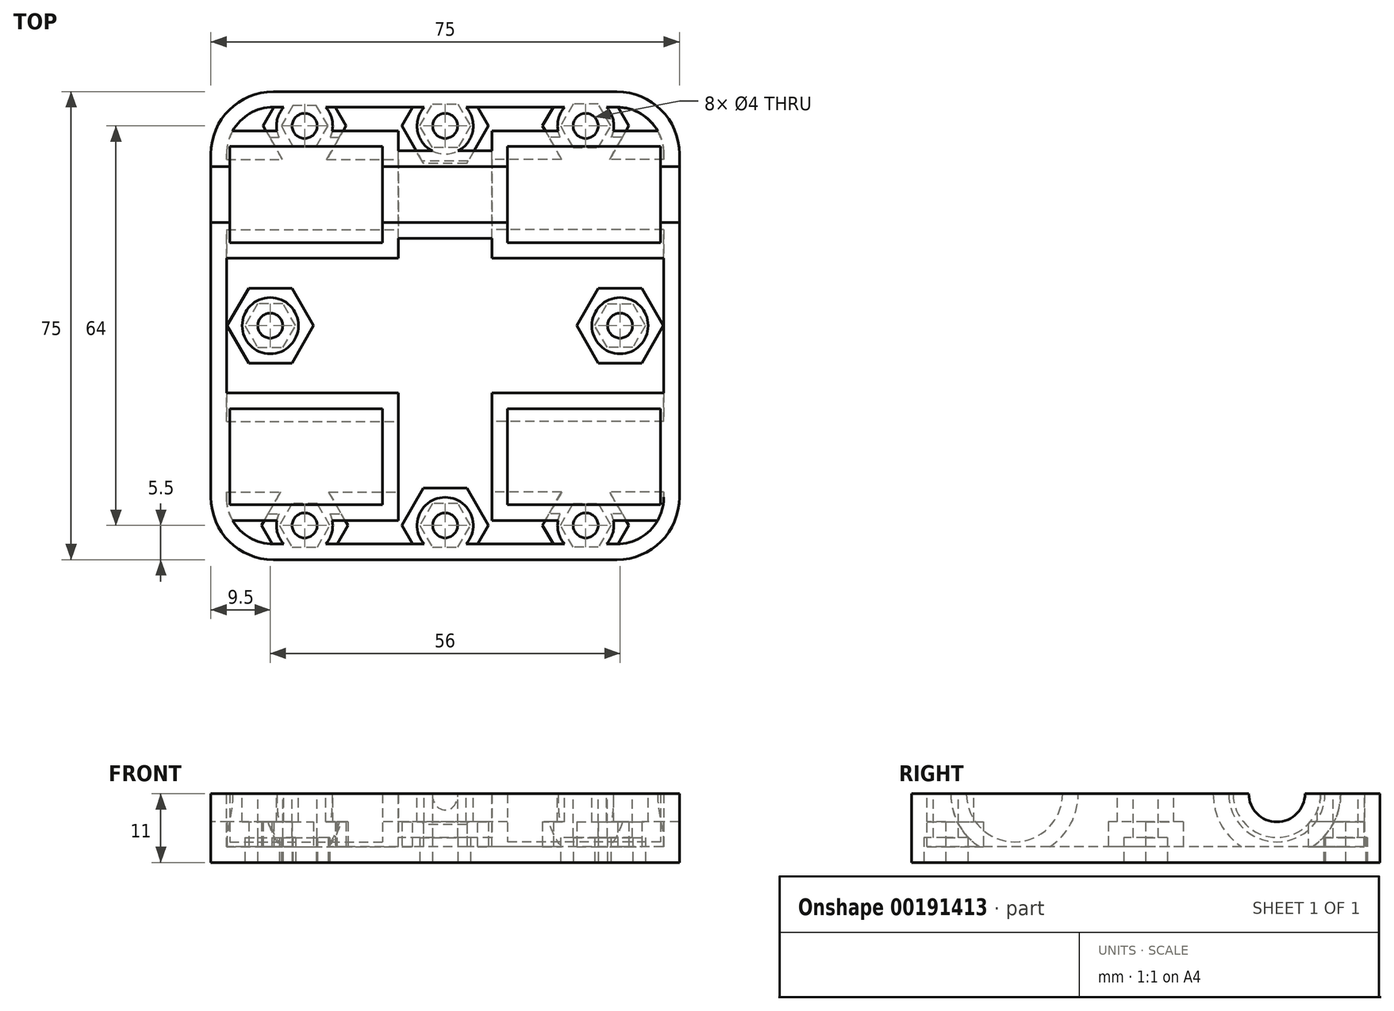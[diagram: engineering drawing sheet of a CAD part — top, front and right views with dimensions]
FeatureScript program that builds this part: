
annotation { "Feature Type Name" : "Feature", "Feature Type Description" : "" }
export const myFeature = defineFeature(function(context is Context, id is Id, definition is map)
    precondition{}
    {
        {
            var Q0;
            Q0=qCreatedBy(makeId("Top.planeOp"),FACE);
            var sketch = newSketch(context, id + "F0", { "sketchPlane" : qUnion([Q0])});
            skLineSegment(sketch, "E0.bottom", {"start": v(37.5, 37.5) * mm, "end": v(-37.5, 37.5) * mm});
            skLineSegment(sketch, "E0.top", {"start": v(37.5, -37.5) * mm, "end": v(-37.5, -37.5) * mm});
            skLineSegment(sketch, "E0.left", {"start": v(37.5, 37.5) * mm, "end": v(37.5, -37.5) * mm});
            skLineSegment(sketch, "E0.right", {"start": v(-37.5, 37.5) * mm, "end": v(-37.5, -37.5) * mm});
            skPoint(sketch, "E0.middle", {"position": v(0, 0) * mm});
            skSolve(sketch);
        }
        {
            var Q0;
            Q0 = qSketchRegion(id + "F0", true);
            extrude(context, id + "F1", {"entities" : qUnion([Q0]), "depth" : 11 * mm});
        }
        {
            var Q0;
            Q0=qCreatedBy(makeId("Right.planeOp"),FACE);
            cPlane(context, id + "F2", {"entities" : qUnion([Q0]), "cplaneType" : CPlaneType.OFFSET, "offset" : 10 * mm, "width" : 150 * mm, "height" : 150 * mm});
        }
        {
            var Q0;
            Q0=qCreatedBy(id+"F2.planeOp",FACE);
            var sketch = newSketch(context, id + "F3", { "sketchPlane" : qUnion([Q0])});
            skLineSegment(sketch, "E1", {"start": v(-21, 26.8) * mm, "end": v(-21, -8.17) * mm, "construction": true});
            skLineSegment(sketch, "E2.MirrorCS", {"start": v(21, 26.8) * mm, "end": v(21, -8.17) * mm, "construction": true});
            skCircle(sketch, "E3", {"center": v(-21, 11) * mm, "radius": 7.7 * mm});
            skCircle(sketch, "E4.MirrorC", {"center": v(21, 11) * mm, "radius": 7.7 * mm});
            skSolve(sketch);
        }
        {
            var Q0;
            Q0 = qSketchRegion(id + "F3", true);
            extrude(context, id + "F4", {"entities" : qUnion([Q0]), "operationType" : NewBodyOperationType.REMOVE, "depth" : 24.5 * mm});
        }
        {
            var Q0;
            Q0=qCreatedBy(makeId("Right.planeOp"),FACE);
            cPlane(context, id + "F5", {"entities" : qUnion([Q0]), "cplaneType" : CPlaneType.OFFSET, "offset" : 10 * mm, "oppositeDirection" : true, "width" : 150 * mm, "height" : 150 * mm});
        }
        {
            var Q0;
            Q0=qCreatedBy(id+"F5.planeOp",FACE);
            var sketch = newSketch(context, id + "F6", { "sketchPlane" : qUnion([Q0])});
            skLineSegment(sketch, "E5", {"start": v(21, 27.18) * mm, "end": v(21, -19.17) * mm, "construction": true});
            skCircle(sketch, "E6", {"center": v(21, 11) * mm, "radius": 7.7 * mm});
            skCircle(sketch, "E7.MirrorC", {"center": v(-21, 11) * mm, "radius": 7.7 * mm});
            skSolve(sketch);
        }
        {
            var Q0;
            Q0 = qSketchRegion(id + "F6", true);
            extrude(context, id + "F7", {"entities" : qUnion([Q0]), "operationType" : NewBodyOperationType.REMOVE, "oppositeDirection" : true, "depth" : 24.5 * mm});
        }
        {
            var Q0;
            Q0=makeQuery(id+"F1.opExtrude","SWEPT_FACE",FACE,{"disambiguationData":[OSD([sQuery(id+"F0.wireOp",EDGE,"E0.right")])]});
            var sketch = newSketch(context, id + "F8", { "sketchPlane" : qUnion([Q0])});
            skLineSegment(sketch, "E8", {"start": v(-21, 26.36) * mm, "end": v(-21, 10.36) * mm, "construction": true});
            skCircle(sketch, "E9", {"center": v(-21, 11) * mm, "radius": 4.5 * mm});
            skPoint(sketch, "E9.centerSnap0", {"position": v(-21, 18.36) * mm});
            skLineSegment(sketch, "E10.MirrorCS", {"start": v(21, 26.36) * mm, "end": v(21, 10.36) * mm, "construction": true});
            skCircle(sketch, "E11.MirrorC", {"center": v(21, 11) * mm, "radius": 4.5 * mm});
            skSolve(sketch);
        }
        {
            var Q0;
            {var subQ0=sQuery(id+"F8.wireOp",EDGE,"E9");var subQ1=makeQuery(id+"F1.opExtrude","CAP_EDGE",EDGE,{"disambiguationData":[OSD([sQuery(id+"F0.wireOp",EDGE,"E0.right")])],"isStart":false});var subQ2=makeQuery(id+"F8.imprint","INTERSECT",VERTEX,{"disambiguationData":[OD(0.0)],"derivedFrom":[subQ1,subQ0]});Q0=makeQuery(id+"F8.imprint","IMPRINT",FACE,{"disambiguationData":[TD([[makeQuery(id+"F8.imprint","IMPRINT",EDGE,{"disambiguationData":[TD([[subQ2,1.0]])],"derivedFrom":subQ0}),1.0]])]});}
            var Q1;
            {var subQ0=sQuery(id+"F8.wireOp",EDGE,"E9");var subQ1=makeQuery(id+"F1.opExtrude","CAP_EDGE",EDGE,{"disambiguationData":[OSD([sQuery(id+"F0.wireOp",EDGE,"E0.right")])],"isStart":false});var subQ2=makeQuery(id+"F8.imprint","INTERSECT",VERTEX,{"disambiguationData":[OD(0.0)],"derivedFrom":[subQ1,subQ0]});Q1=makeQuery(id+"F8.imprint","IMPRINT",FACE,{"disambiguationData":[TD([[makeQuery(id+"F8.imprint","IMPRINT",EDGE,{"disambiguationData":[TD([[subQ2,-1.0]])],"derivedFrom":subQ0}),1.0]])]});}
            var Q2;
            {var subQ0=sQuery(id+"F8.wireOp",EDGE,"E11.MirrorC");var subQ1=makeQuery(id+"F1.opExtrude","CAP_EDGE",EDGE,{"disambiguationData":[OSD([sQuery(id+"F0.wireOp",EDGE,"E0.right")])],"isStart":false});var subQ2=makeQuery(id+"F8.imprint","INTERSECT",VERTEX,{"disambiguationData":[OD(0.0)],"derivedFrom":[subQ1,subQ0]});Q2=makeQuery(id+"F8.imprint","IMPRINT",FACE,{"disambiguationData":[TD([[makeQuery(id+"F8.imprint","IMPRINT",EDGE,{"disambiguationData":[TD([[subQ2,-1.0]])],"derivedFrom":subQ0}),-1.0]])]});}
            extrude(context, id + "F9", {"entities" : qUnion([Q0, Q1, Q2]), "operationType" : NewBodyOperationType.REMOVE, "endBound" : BoundingType.THROUGH_ALL, "oppositeDirection" : true, "depth" : 25 * mm});
        }
        {
            var Q0;
            {var subQ0=sQuery(id+"F6.wireOp",EDGE,"E6");var subQ1=sQuery(id+"F3.wireOp",EDGE,"E4.MirrorC");var subQ2=sQuery(id+"F6.wireOp",EDGE,"E7.MirrorC");var subQ3=sQuery(id+"F3.wireOp",EDGE,"E3");var subQ4=sQuery(id+"F0.wireOp",EDGE,"E0.right");var subQ5=sQuery(id+"F0.wireOp",EDGE,"E0.left");Q0=makeQuery(id+"F9.boolean.opBoolean","SPLIT",FACE,{"disambiguationData":[TD([makeQuery(id+"F1.opExtrude","SWEPT_FACE",FACE,{"disambiguationData":[OSD([subQ5])]}),makeQuery(id+"F1.opExtrude","SWEPT_FACE",FACE,{"disambiguationData":[OSD([subQ4])]}),makeQuery(id+"F4.boolean.opBoolean","COPY",FACE,{"derivedFrom":makeQuery(id+"F4.opExtrude","SWEPT_FACE",FACE,{"disambiguationData":[OSD([subQ3])]})}),makeQuery(id+"F4.boolean.opBoolean","COPY",FACE,{"derivedFrom":makeQuery(id+"F4.opExtrude","CAP_FACE",FACE,{"disambiguationData":[OSD([subQ3])],"isStart":true})}),makeQuery(id+"F4.boolean.opBoolean","COPY",FACE,{"derivedFrom":makeQuery(id+"F4.opExtrude","CAP_FACE",FACE,{"disambiguationData":[OSD([subQ3])],"isStart":false})}),makeQuery(id+"F4.boolean.opBoolean","COPY",FACE,{"derivedFrom":makeQuery(id+"F4.opExtrude","SWEPT_FACE",FACE,{"disambiguationData":[OSD([subQ1])]})}),makeQuery(id+"F4.boolean.opBoolean","COPY",FACE,{"derivedFrom":makeQuery(id+"F4.opExtrude","CAP_FACE",FACE,{"disambiguationData":[OSD([subQ1])],"isStart":true})}),makeQuery(id+"F4.boolean.opBoolean","COPY",FACE,{"derivedFrom":makeQuery(id+"F4.opExtrude","CAP_FACE",FACE,{"disambiguationData":[OSD([subQ1])],"isStart":false})}),makeQuery(id+"F7.boolean.opBoolean","COPY",FACE,{"derivedFrom":makeQuery(id+"F7.opExtrude","SWEPT_FACE",FACE,{"disambiguationData":[OSD([subQ0])]})}),makeQuery(id+"F7.boolean.opBoolean","COPY",FACE,{"derivedFrom":makeQuery(id+"F7.opExtrude","CAP_FACE",FACE,{"disambiguationData":[OSD([subQ0])],"isStart":true})}),makeQuery(id+"F7.boolean.opBoolean","COPY",FACE,{"derivedFrom":makeQuery(id+"F7.opExtrude","CAP_FACE",FACE,{"disambiguationData":[OSD([subQ0])],"isStart":false})}),makeQuery(id+"F7.boolean.opBoolean","COPY",FACE,{"derivedFrom":makeQuery(id+"F7.opExtrude","SWEPT_FACE",FACE,{"disambiguationData":[OSD([subQ2])]})}),makeQuery(id+"F7.boolean.opBoolean","COPY",FACE,{"derivedFrom":makeQuery(id+"F7.opExtrude","CAP_FACE",FACE,{"disambiguationData":[OSD([subQ2])],"isStart":true})}),makeQuery(id+"F7.boolean.opBoolean","COPY",FACE,{"derivedFrom":makeQuery(id+"F7.opExtrude","CAP_FACE",FACE,{"disambiguationData":[OSD([subQ2])],"isStart":false})}),makeQuery(id+"F9.opExtrude","SWEPT_FACE",FACE,{"disambiguationData":[OSD([sQuery(id+"F8.wireOp",EDGE,"E9")])]}),makeQuery(id+"F9.opExtrude","SWEPT_FACE",FACE,{"disambiguationData":[OSD([sQuery(id+"F8.wireOp",EDGE,"E11.MirrorC")])]})])],"derivedFrom":makeQuery(id+"F1.opExtrude","CAP_FACE",FACE,{"disambiguationData":[OSD([sQuery(id+"F0.wireOp",EDGE,"E0.bottom"),sQuery(id+"F0.wireOp",EDGE,"E0.top"),subQ5,subQ4])],"isStart":false})});}
            var sketch = newSketch(context, id + "F10", { "sketchPlane" : qUnion([Q0])});
            skCircle(sketch, "E12", {"center": v(28, 0) * mm, "radius": 2 * mm});
            skCircle(sketch, "E13.MirrorC", {"center": v(-28, 0) * mm, "radius": 2 * mm});
            skCircle(sketch, "E14", {"center": v(0, -32) * mm, "radius": 2 * mm});
            skCircle(sketch, "E15.MirrorC", {"center": v(0, 32) * mm, "radius": 2 * mm});
            skCircle(sketch, "E16", {"center": v(-22.5, 32) * mm, "radius": 2 * mm});
            skCircle(sketch, "E17.MirrorC", {"center": v(22.5, 32) * mm, "radius": 2 * mm});
            skCircle(sketch, "E18.MirrorC", {"center": v(-22.5, -32) * mm, "radius": 2 * mm});
            skCircle(sketch, "E19.MirrorC", {"center": v(22.5, -32) * mm, "radius": 2 * mm});
            skSolve(sketch);
        }
        {
            var Q0;
            Q0 = qSketchRegion(id + "F10", true);
            extrude(context, id + "F11", {"entities" : qUnion([Q0]), "operationType" : NewBodyOperationType.REMOVE, "endBound" : BoundingType.THROUGH_ALL, "oppositeDirection" : true, "depth" : 25 * mm});
        }
        {
            var Q0;
            Q0=makeQuery(id+"F1.opExtrude","SWEPT_EDGE",EDGE,{"disambiguationData":[OSD([sQuery(id+"F0.wireOp",EDGE,"E0.bottom"),sQuery(id+"F0.wireOp",EDGE,"E0.left")])]});
            var Q1;
            Q1=makeQuery(id+"F1.opExtrude","SWEPT_EDGE",EDGE,{"disambiguationData":[OSD([sQuery(id+"F0.wireOp",EDGE,"E0.top"),sQuery(id+"F0.wireOp",EDGE,"E0.left")])]});
            var Q2;
            Q2=makeQuery(id+"F1.opExtrude","SWEPT_EDGE",EDGE,{"disambiguationData":[OSD([sQuery(id+"F0.wireOp",EDGE,"E0.top"),sQuery(id+"F0.wireOp",EDGE,"E0.right")])]});
            var Q3;
            Q3=makeQuery(id+"F1.opExtrude","SWEPT_EDGE",EDGE,{"disambiguationData":[OSD([sQuery(id+"F0.wireOp",EDGE,"E0.bottom"),sQuery(id+"F0.wireOp",EDGE,"E0.right")])]});
            fillet(context, id + "F12", {"entities" : qUnion([Q0, Q1, Q2, Q3]), "radius" : 10 * mm, "tangentPropagation" : true, "allowEdgeOverflow" : false});
        }
        {
            var Q0;
            Q0=makeQuery(id+"F1.opExtrude","CAP_FACE",FACE,{"disambiguationData":[OSD([sQuery(id+"F0.wireOp",EDGE,"E0.bottom"),sQuery(id+"F0.wireOp",EDGE,"E0.top"),sQuery(id+"F0.wireOp",EDGE,"E0.left"),sQuery(id+"F0.wireOp",EDGE,"E0.right")])],"isStart":true});
            var sketch = newSketch(context, id + "F13", { "sketchPlane" : qUnion([Q0])});
            skCircle(sketch, "E20.cCircle", {"center": v(-22.5, 32) * mm, "radius": 3.5 * mm, "construction": true});
            skLineSegment(sketch, "E20.0", {"start": v(-24.52, 35.5) * mm, "end": v(-20.48, 35.5) * mm});
            skLineSegment(sketch, "E20.1", {"start": v(-20.48, 35.5) * mm, "end": v(-18.46, 32) * mm});
            skLineSegment(sketch, "E20.2", {"start": v(-18.46, 32) * mm, "end": v(-20.48, 28.5) * mm});
            skLineSegment(sketch, "E20.3", {"start": v(-20.48, 28.5) * mm, "end": v(-24.52, 28.5) * mm});
            skLineSegment(sketch, "E20.4", {"start": v(-24.52, 28.5) * mm, "end": v(-26.54, 32) * mm});
            skLineSegment(sketch, "E20.5", {"start": v(-26.54, 32) * mm, "end": v(-24.52, 35.5) * mm});
            skPoint(sketch, "E20.0.midPoint", {"position": v(-22.5, 35.5) * mm});
            skLineSegment(sketch, "E21.MirrorCS", {"start": v(24.52, 35.5) * mm, "end": v(20.48, 35.5) * mm});
            skLineSegment(sketch, "E22.MirrorCS", {"start": v(26.54, 32) * mm, "end": v(24.52, 35.5) * mm});
            skLineSegment(sketch, "E23.MirrorCS", {"start": v(20.48, 28.5) * mm, "end": v(24.52, 28.5) * mm});
            skLineSegment(sketch, "E24.MirrorCS", {"start": v(18.46, 32) * mm, "end": v(20.48, 28.5) * mm});
            skCircle(sketch, "E25.MirrorC", {"center": v(22.5, 32) * mm, "radius": 3.5 * mm, "construction": true});
            skPoint(sketch, "E26.MirrorP", {"position": v(22.5, 35.5) * mm});
            skLineSegment(sketch, "E27.MirrorCS", {"start": v(24.52, 28.5) * mm, "end": v(26.54, 32) * mm});
            skLineSegment(sketch, "E28.MirrorCS", {"start": v(20.48, 35.5) * mm, "end": v(18.46, 32) * mm});
            skLineSegment(sketch, "E29.MirrorCS", {"start": v(24.52, -28.5) * mm, "end": v(26.54, -32) * mm});
            skLineSegment(sketch, "E30.MirrorCS", {"start": v(24.52, -35.5) * mm, "end": v(20.48, -35.5) * mm});
            skLineSegment(sketch, "E31.MirrorCS", {"start": v(18.46, -32) * mm, "end": v(20.48, -28.5) * mm});
            skLineSegment(sketch, "E32.MirrorCS", {"start": v(20.48, -28.5) * mm, "end": v(24.52, -28.5) * mm});
            skLineSegment(sketch, "E33.MirrorCS", {"start": v(26.54, -32) * mm, "end": v(24.52, -35.5) * mm});
            skLineSegment(sketch, "E34.MirrorCS", {"start": v(20.48, -35.5) * mm, "end": v(18.46, -32) * mm});
            skCircle(sketch, "E35.MirrorC", {"center": v(22.5, -32) * mm, "radius": 3.5 * mm, "construction": true});
            skPoint(sketch, "E36.MirrorP", {"position": v(22.5, -35.5) * mm});
            skCircle(sketch, "E37.cCircle", {"center": v(-22.5, -32) * mm, "radius": 3.25 * mm, "construction": true});
            skLineSegment(sketch, "E37.0", {"start": v(-24.38, -28.75) * mm, "end": v(-20.62, -28.75) * mm});
            skLineSegment(sketch, "E37.1", {"start": v(-20.62, -28.75) * mm, "end": v(-18.75, -32) * mm});
            skLineSegment(sketch, "E37.2", {"start": v(-18.75, -32) * mm, "end": v(-20.62, -35.25) * mm});
            skLineSegment(sketch, "E37.3", {"start": v(-20.62, -35.25) * mm, "end": v(-24.38, -35.25) * mm});
            skLineSegment(sketch, "E37.4", {"start": v(-24.38, -35.25) * mm, "end": v(-26.25, -32) * mm});
            skLineSegment(sketch, "E37.5", {"start": v(-26.25, -32) * mm, "end": v(-24.38, -28.75) * mm});
            skPoint(sketch, "E37.0.midPoint", {"position": v(-22.5, -28.75) * mm});
            skCircle(sketch, "E38.cCircle", {"center": v(0, 32) * mm, "radius": 3.5 * mm, "construction": true});
            skLineSegment(sketch, "E38.0", {"start": v(-2.02, 35.5) * mm, "end": v(2.02, 35.5) * mm});
            skLineSegment(sketch, "E38.1", {"start": v(2.02, 35.5) * mm, "end": v(4.04, 32) * mm});
            skLineSegment(sketch, "E38.2", {"start": v(4.04, 32) * mm, "end": v(2.02, 28.5) * mm});
            skLineSegment(sketch, "E38.3", {"start": v(2.02, 28.5) * mm, "end": v(-2.02, 28.5) * mm});
            skLineSegment(sketch, "E38.4", {"start": v(-2.02, 28.5) * mm, "end": v(-4.04, 32) * mm});
            skLineSegment(sketch, "E38.5", {"start": v(-4.04, 32) * mm, "end": v(-2.02, 35.5) * mm});
            skPoint(sketch, "E38.0.midPoint", {"position": v(0, 35.5) * mm});
            skCircle(sketch, "E39.cCircle", {"center": v(-28, 0) * mm, "radius": 3.5 * mm, "construction": true});
            skLineSegment(sketch, "E39.0", {"start": v(-30.02, 3.5) * mm, "end": v(-25.98, 3.5) * mm});
            skLineSegment(sketch, "E39.1", {"start": v(-25.98, 3.5) * mm, "end": v(-23.96, 0) * mm});
            skLineSegment(sketch, "E39.2", {"start": v(-23.96, 0) * mm, "end": v(-25.98, -3.5) * mm});
            skLineSegment(sketch, "E39.3", {"start": v(-25.98, -3.5) * mm, "end": v(-30.02, -3.5) * mm});
            skLineSegment(sketch, "E39.4", {"start": v(-30.02, -3.5) * mm, "end": v(-32.04, 0) * mm});
            skLineSegment(sketch, "E39.5", {"start": v(-32.04, 0) * mm, "end": v(-30.02, 3.5) * mm});
            skPoint(sketch, "E39.0.midPoint", {"position": v(-28, 3.5) * mm});
            skLineSegment(sketch, "E40.MirrorCS", {"start": v(30.02, 3.5) * mm, "end": v(25.98, 3.5) * mm});
            skLineSegment(sketch, "E41.MirrorCS", {"start": v(25.98, -3.5) * mm, "end": v(30.02, -3.5) * mm});
            skLineSegment(sketch, "E42.MirrorCS", {"start": v(30.02, -3.5) * mm, "end": v(32.04, 0) * mm});
            skLineSegment(sketch, "E43.MirrorCS", {"start": v(25.98, 3.5) * mm, "end": v(23.96, 0) * mm});
            skLineSegment(sketch, "E44.MirrorCS", {"start": v(23.96, 0) * mm, "end": v(25.98, -3.5) * mm});
            skLineSegment(sketch, "E45.MirrorCS", {"start": v(32.04, 0) * mm, "end": v(30.02, 3.5) * mm});
            skCircle(sketch, "E46.MirrorC", {"center": v(28, 0) * mm, "radius": 3.5 * mm, "construction": true});
            skPoint(sketch, "E47.MirrorP", {"position": v(28, 3.5) * mm});
            skLineSegment(sketch, "E48.MirrorCS", {"start": v(2.02, -35.5) * mm, "end": v(4.04, -32) * mm});
            skLineSegment(sketch, "E49.MirrorCS", {"start": v(2.02, -28.5) * mm, "end": v(-2.02, -28.5) * mm});
            skPoint(sketch, "E50.MirrorP", {"position": v(0, -35.5) * mm});
            skLineSegment(sketch, "E51.MirrorCS", {"start": v(-2.02, -28.5) * mm, "end": v(-4.04, -32) * mm});
            skCircle(sketch, "E52.MirrorC", {"center": v(0, -32) * mm, "radius": 3.5 * mm, "construction": true});
            skLineSegment(sketch, "E53.MirrorCS", {"start": v(-2.02, -35.5) * mm, "end": v(2.02, -35.5) * mm});
            skLineSegment(sketch, "E54.MirrorCS", {"start": v(-4.04, -32) * mm, "end": v(-2.02, -35.5) * mm});
            skLineSegment(sketch, "E55.MirrorCS", {"start": v(4.04, -32) * mm, "end": v(2.02, -28.5) * mm});
            skSolve(sketch);
        }
        {
            var Q0;
            Q0 = qSketchRegion(id + "F13", true);
            extrude(context, id + "F14", {"entities" : qUnion([Q0]), "operationType" : NewBodyOperationType.REMOVE, "oppositeDirection" : true, "depth" : 4 * mm});
        }
        {
            var Q0;
            {var subQ0=sQuery(id+"F3.wireOp",EDGE,"E4.MirrorC");var subQ1=sQuery(id+"F0.wireOp",EDGE,"E0.right");var subQ2=sQuery(id+"F0.wireOp",EDGE,"E0.left");var subQ3=sQuery(id+"F0.wireOp",EDGE,"E0.bottom");var subQ4=sQuery(id+"F6.wireOp",EDGE,"E6");Q0=makeQuery(id+"F9.boolean.opBoolean","SPLIT",FACE,{"disambiguationData":[TD([makeQuery(id+"F1.opExtrude","SWEPT_FACE",FACE,{"disambiguationData":[OSD([subQ3])]}),makeQuery(id+"F1.opExtrude","SWEPT_FACE",FACE,{"disambiguationData":[OSD([subQ2])]}),makeQuery(id+"F1.opExtrude","SWEPT_FACE",FACE,{"disambiguationData":[OSD([subQ1])]}),makeQuery(id+"F4.boolean.opBoolean","COPY",FACE,{"derivedFrom":makeQuery(id+"F4.opExtrude","SWEPT_FACE",FACE,{"disambiguationData":[OSD([subQ0])]})}),makeQuery(id+"F4.boolean.opBoolean","COPY",FACE,{"derivedFrom":makeQuery(id+"F4.opExtrude","CAP_FACE",FACE,{"disambiguationData":[OSD([subQ0])],"isStart":true})}),makeQuery(id+"F4.boolean.opBoolean","COPY",FACE,{"derivedFrom":makeQuery(id+"F4.opExtrude","CAP_FACE",FACE,{"disambiguationData":[OSD([subQ0])],"isStart":false})}),makeQuery(id+"F7.boolean.opBoolean","COPY",FACE,{"derivedFrom":makeQuery(id+"F7.opExtrude","SWEPT_FACE",FACE,{"disambiguationData":[OSD([subQ4])]})}),makeQuery(id+"F7.boolean.opBoolean","COPY",FACE,{"derivedFrom":makeQuery(id+"F7.opExtrude","CAP_FACE",FACE,{"disambiguationData":[OSD([subQ4])],"isStart":true})}),makeQuery(id+"F7.boolean.opBoolean","COPY",FACE,{"derivedFrom":makeQuery(id+"F7.opExtrude","CAP_FACE",FACE,{"disambiguationData":[OSD([subQ4])],"isStart":false})}),makeQuery(id+"F9.opExtrude","SWEPT_FACE",FACE,{"disambiguationData":[OSD([sQuery(id+"F8.wireOp",EDGE,"E9")])]})])],"derivedFrom":makeQuery(id+"F1.opExtrude","CAP_FACE",FACE,{"disambiguationData":[OSD([subQ3,sQuery(id+"F0.wireOp",EDGE,"E0.top"),subQ2,subQ1])],"isStart":false})});}
            var Q1;
            {var subQ0=sQuery(id+"F6.wireOp",EDGE,"E6");var subQ1=sQuery(id+"F3.wireOp",EDGE,"E4.MirrorC");var subQ2=sQuery(id+"F6.wireOp",EDGE,"E7.MirrorC");var subQ3=sQuery(id+"F3.wireOp",EDGE,"E3");var subQ4=sQuery(id+"F0.wireOp",EDGE,"E0.right");var subQ5=sQuery(id+"F0.wireOp",EDGE,"E0.left");Q1=makeQuery(id+"F9.boolean.opBoolean","SPLIT",FACE,{"disambiguationData":[TD([makeQuery(id+"F1.opExtrude","SWEPT_FACE",FACE,{"disambiguationData":[OSD([subQ5])]}),makeQuery(id+"F1.opExtrude","SWEPT_FACE",FACE,{"disambiguationData":[OSD([subQ4])]}),makeQuery(id+"F4.boolean.opBoolean","COPY",FACE,{"derivedFrom":makeQuery(id+"F4.opExtrude","SWEPT_FACE",FACE,{"disambiguationData":[OSD([subQ3])]})}),makeQuery(id+"F4.boolean.opBoolean","COPY",FACE,{"derivedFrom":makeQuery(id+"F4.opExtrude","CAP_FACE",FACE,{"disambiguationData":[OSD([subQ3])],"isStart":true})}),makeQuery(id+"F4.boolean.opBoolean","COPY",FACE,{"derivedFrom":makeQuery(id+"F4.opExtrude","CAP_FACE",FACE,{"disambiguationData":[OSD([subQ3])],"isStart":false})}),makeQuery(id+"F4.boolean.opBoolean","COPY",FACE,{"derivedFrom":makeQuery(id+"F4.opExtrude","SWEPT_FACE",FACE,{"disambiguationData":[OSD([subQ1])]})}),makeQuery(id+"F4.boolean.opBoolean","COPY",FACE,{"derivedFrom":makeQuery(id+"F4.opExtrude","CAP_FACE",FACE,{"disambiguationData":[OSD([subQ1])],"isStart":true})}),makeQuery(id+"F4.boolean.opBoolean","COPY",FACE,{"derivedFrom":makeQuery(id+"F4.opExtrude","CAP_FACE",FACE,{"disambiguationData":[OSD([subQ1])],"isStart":false})}),makeQuery(id+"F7.boolean.opBoolean","COPY",FACE,{"derivedFrom":makeQuery(id+"F7.opExtrude","SWEPT_FACE",FACE,{"disambiguationData":[OSD([subQ0])]})}),makeQuery(id+"F7.boolean.opBoolean","COPY",FACE,{"derivedFrom":makeQuery(id+"F7.opExtrude","CAP_FACE",FACE,{"disambiguationData":[OSD([subQ0])],"isStart":true})}),makeQuery(id+"F7.boolean.opBoolean","COPY",FACE,{"derivedFrom":makeQuery(id+"F7.opExtrude","CAP_FACE",FACE,{"disambiguationData":[OSD([subQ0])],"isStart":false})}),makeQuery(id+"F7.boolean.opBoolean","COPY",FACE,{"derivedFrom":makeQuery(id+"F7.opExtrude","SWEPT_FACE",FACE,{"disambiguationData":[OSD([subQ2])]})}),makeQuery(id+"F7.boolean.opBoolean","COPY",FACE,{"derivedFrom":makeQuery(id+"F7.opExtrude","CAP_FACE",FACE,{"disambiguationData":[OSD([subQ2])],"isStart":true})}),makeQuery(id+"F7.boolean.opBoolean","COPY",FACE,{"derivedFrom":makeQuery(id+"F7.opExtrude","CAP_FACE",FACE,{"disambiguationData":[OSD([subQ2])],"isStart":false})}),makeQuery(id+"F9.opExtrude","SWEPT_FACE",FACE,{"disambiguationData":[OSD([sQuery(id+"F8.wireOp",EDGE,"E9")])]}),makeQuery(id+"F9.opExtrude","SWEPT_FACE",FACE,{"disambiguationData":[OSD([sQuery(id+"F8.wireOp",EDGE,"E11.MirrorC")])]})])],"derivedFrom":makeQuery(id+"F1.opExtrude","CAP_FACE",FACE,{"disambiguationData":[OSD([sQuery(id+"F0.wireOp",EDGE,"E0.bottom"),sQuery(id+"F0.wireOp",EDGE,"E0.top"),subQ5,subQ4])],"isStart":false})});}
            var Q2;
            {var subQ0=sQuery(id+"F3.wireOp",EDGE,"E3");var subQ1=sQuery(id+"F0.wireOp",EDGE,"E0.left");var subQ2=sQuery(id+"F0.wireOp",EDGE,"E0.right");var subQ3=sQuery(id+"F0.wireOp",EDGE,"E0.top");var subQ4=sQuery(id+"F6.wireOp",EDGE,"E7.MirrorC");Q2=makeQuery(id+"F9.boolean.opBoolean","SPLIT",FACE,{"disambiguationData":[TD([makeQuery(id+"F1.opExtrude","SWEPT_FACE",FACE,{"disambiguationData":[OSD([subQ3])]}),makeQuery(id+"F1.opExtrude","SWEPT_FACE",FACE,{"disambiguationData":[OSD([subQ1])]}),makeQuery(id+"F1.opExtrude","SWEPT_FACE",FACE,{"disambiguationData":[OSD([subQ2])]}),makeQuery(id+"F4.boolean.opBoolean","COPY",FACE,{"derivedFrom":makeQuery(id+"F4.opExtrude","SWEPT_FACE",FACE,{"disambiguationData":[OSD([subQ0])]})}),makeQuery(id+"F4.boolean.opBoolean","COPY",FACE,{"derivedFrom":makeQuery(id+"F4.opExtrude","CAP_FACE",FACE,{"disambiguationData":[OSD([subQ0])],"isStart":true})}),makeQuery(id+"F4.boolean.opBoolean","COPY",FACE,{"derivedFrom":makeQuery(id+"F4.opExtrude","CAP_FACE",FACE,{"disambiguationData":[OSD([subQ0])],"isStart":false})}),makeQuery(id+"F7.boolean.opBoolean","COPY",FACE,{"derivedFrom":makeQuery(id+"F7.opExtrude","SWEPT_FACE",FACE,{"disambiguationData":[OSD([subQ4])]})}),makeQuery(id+"F7.boolean.opBoolean","COPY",FACE,{"derivedFrom":makeQuery(id+"F7.opExtrude","CAP_FACE",FACE,{"disambiguationData":[OSD([subQ4])],"isStart":true})}),makeQuery(id+"F7.boolean.opBoolean","COPY",FACE,{"derivedFrom":makeQuery(id+"F7.opExtrude","CAP_FACE",FACE,{"disambiguationData":[OSD([subQ4])],"isStart":false})}),makeQuery(id+"F9.opExtrude","SWEPT_FACE",FACE,{"disambiguationData":[OSD([sQuery(id+"F8.wireOp",EDGE,"E11.MirrorC")])]})])],"derivedFrom":makeQuery(id+"F1.opExtrude","CAP_FACE",FACE,{"disambiguationData":[OSD([sQuery(id+"F0.wireOp",EDGE,"E0.bottom"),subQ3,subQ1,subQ2])],"isStart":false})});}
            shell(context, id + "F15", {"entities" : qUnion([Q0, Q1, Q2]), "thickness" : 2.5 * mm});
        }
    });
